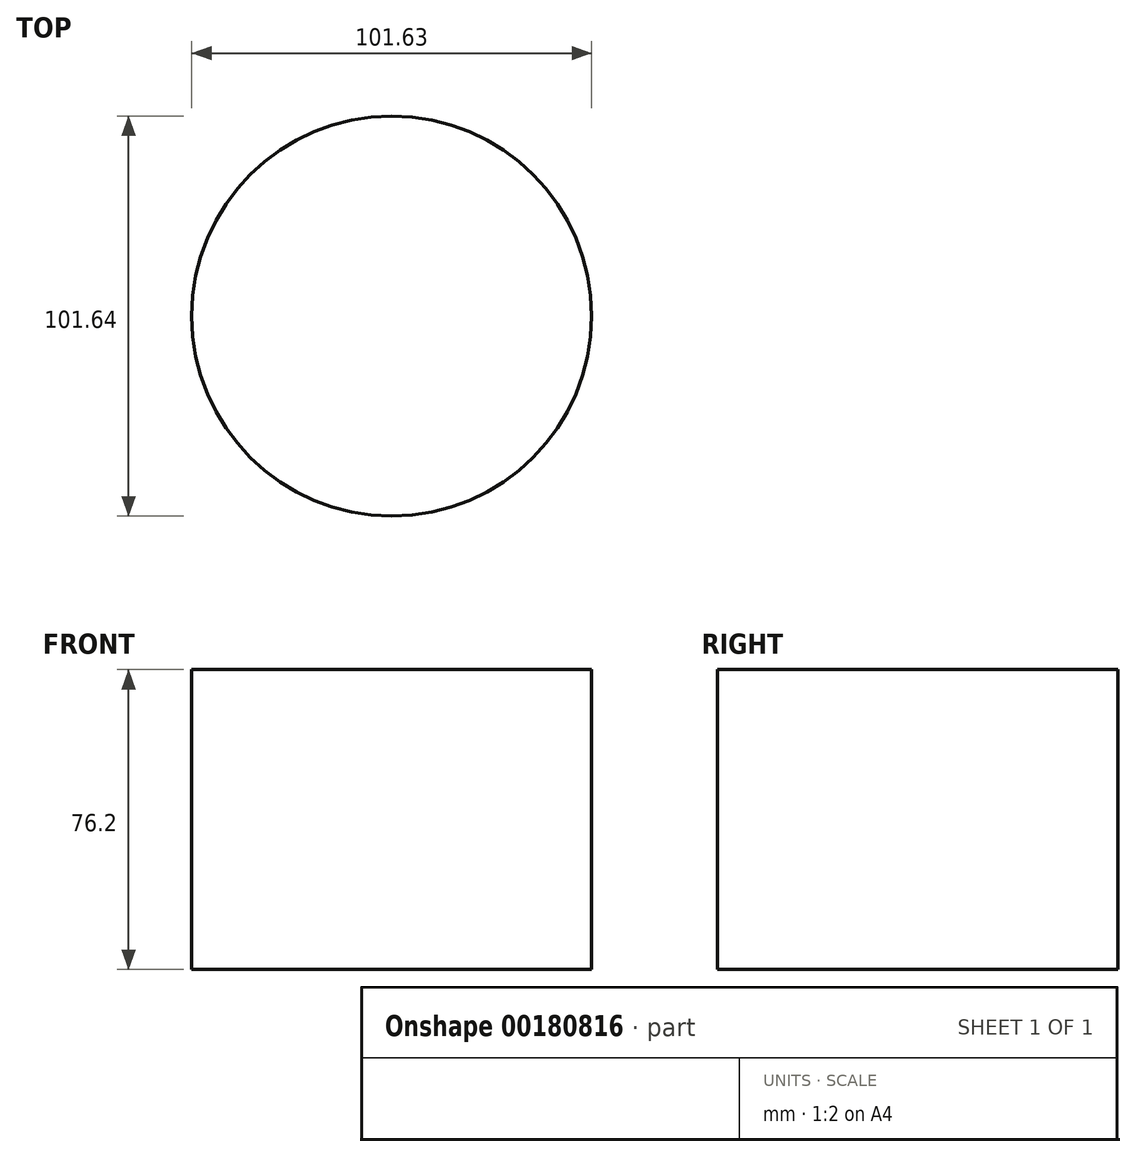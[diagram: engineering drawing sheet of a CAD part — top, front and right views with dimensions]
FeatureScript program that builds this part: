
annotation { "Feature Type Name" : "Feature", "Feature Type Description" : "" }
export const myFeature = defineFeature(function(context is Context, id is Id, definition is map)
    precondition{}
    {
        {
            var Q0;
            Q0=qCreatedBy(makeId("Top.planeOp"),FACE);
            var sketch = newSketch(context, id + "F0", { "sketchPlane" : qUnion([Q0])});
            skCircle(sketch, "E0", {"center": v(0.05, -1.3) * mm, "radius": 50.82 * mm});
            skPoint(sketch, "E0.first.point", {"position": v(-50.75, 0) * mm});
            skPoint(sketch, "E0.second.point", {"position": v(50.85, 0) * mm});
            skPoint(sketch, "E0.third.point", {"position": v(0, 49.53) * mm});
            skSolve(sketch);
        }
        {
            var Q0;
            Q0 = qSketchRegion(id + "F0", true);
            extrude(context, id + "F1", {"entities" : qUnion([Q0]), "depth" : 38.1 * mm});
        }
        {
            var Q0;
            Q0=makeQuery(id+"F1.opExtrude","CAP_FACE",FACE,{"disambiguationData":[OSD([sQuery(id+"F0.wireOp",EDGE,"E0")])],"isStart":true});
            extrude(context, id + "F2", {"entities" : qUnion([Q0]), "operationType" : NewBodyOperationType.ADD, "depth" : 38.1 * mm});
        }
    });
